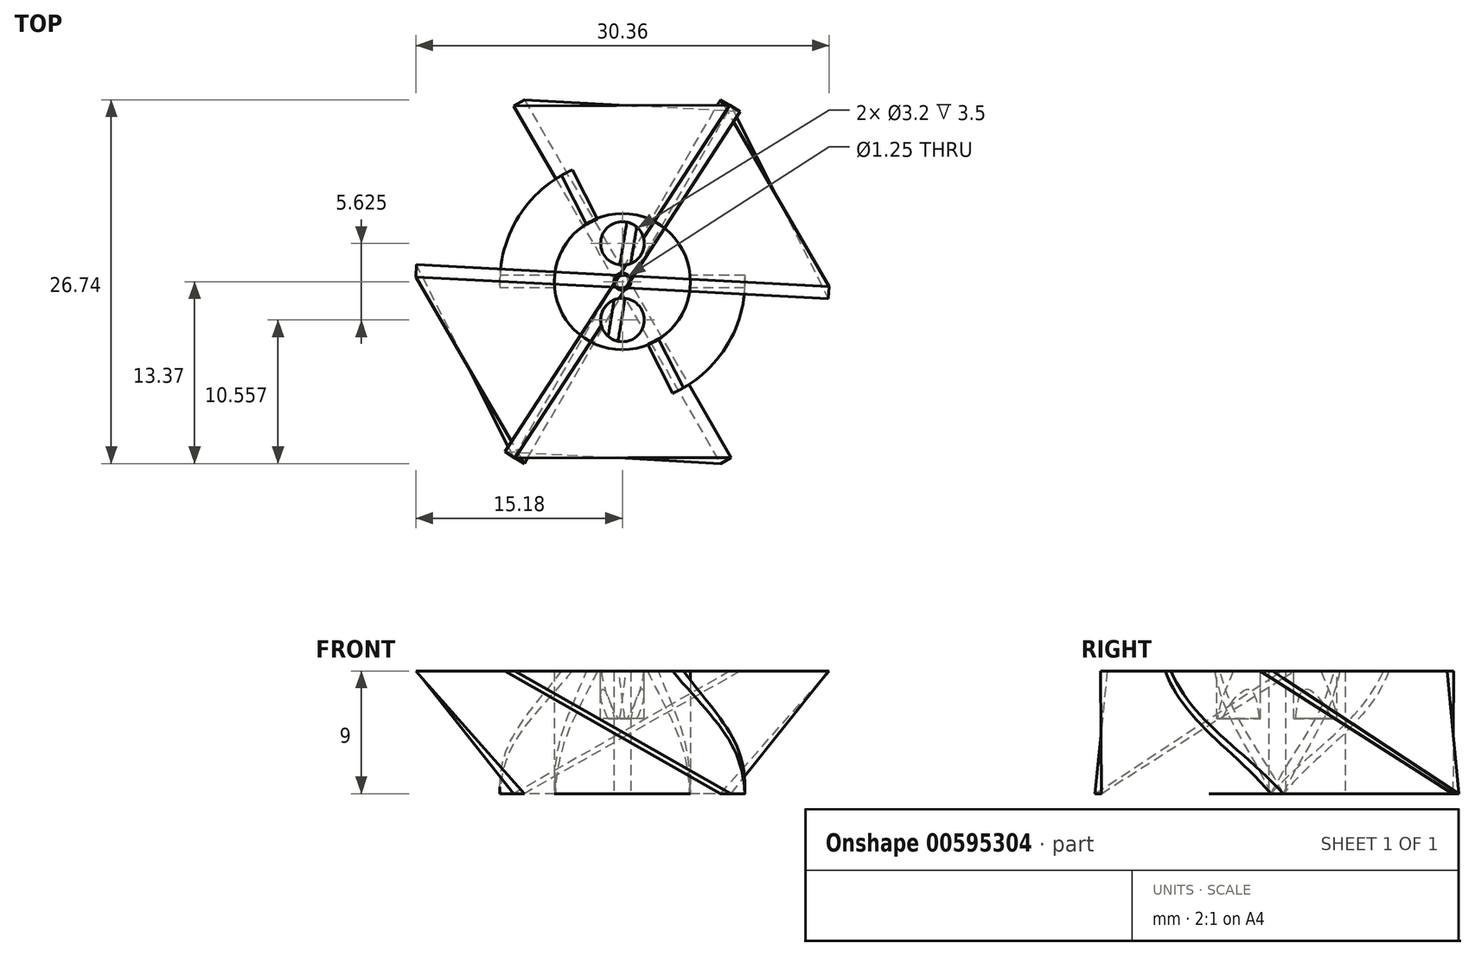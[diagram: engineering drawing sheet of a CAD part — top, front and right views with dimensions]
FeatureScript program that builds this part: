
annotation { "Feature Type Name" : "Feature", "Feature Type Description" : "" }
export const myFeature = defineFeature(function(context is Context, id is Id, definition is map)
    precondition{}
    {
        {
            var Q0;
            Q0=qCreatedBy(makeId("Top.planeOp"),FACE);
            cPlane(context, id + "F0", {"entities" : qUnion([Q0]), "cplaneType" : CPlaneType.OFFSET, "offset" : 9 * mm, "width" : 150 * mm, "height" : 150 * mm});
        }
        {
            var Q0;
            Q0=qCreatedBy(makeId("Top.planeOp"),FACE);
            cPlane(context, id + "F1", {"entities" : qUnion([Q0]), "cplaneType" : CPlaneType.OFFSET, "offset" : 3 * mm, "oppositeDirection" : true, "width" : 150 * mm, "height" : 150 * mm});
        }
        {
            var Q0;
            Q0=qCreatedBy(makeId("Top.planeOp"),FACE);
            var sketch = newSketch(context, id + "F2", { "sketchPlane" : qUnion([Q0])});
            skCircle(sketch, "E0", {"center": v(0, 0) * mm, "radius": 0.63 * mm});
            skCircle(sketch, "E1", {"center": v(0, 0) * mm, "radius": 5 * mm});
            skSolve(sketch);
        }
        {
            var Q0;
            Q0=qCreatedBy(id+"F0.planeOp",FACE);
            var sketch = newSketch(context, id + "F3", { "sketchPlane" : qUnion([Q0])});
            skCircle(sketch, "E2", {"center": v(0, 2.81) * mm, "radius": 1.6 * mm});
            skCircle(sketch, "E3", {"center": v(0, -2.81) * mm, "radius": 1.6 * mm});
            skSolve(sketch);
        }
        {
            var Q0;
            Q0=qCreatedBy(id+"F1.planeOp",FACE);
            var sketch = newSketch(context, id + "F4", { "sketchPlane" : qUnion([Q0])});
            skCircle(sketch, "E4", {"center": v(0, 0) * mm, "radius": 4.95 * mm});
            skCircle(sketch, "E5", {"center": v(0, 0) * mm, "radius": 9 * mm});
            skSolve(sketch);
        }
        {
            var Q0;
            Q0=qCreatedBy(makeId("Top.planeOp"),FACE);
            var sketch = newSketch(context, id + "F5", { "sketchPlane" : qUnion([Q0])});
            skLineSegment(sketch, "E6.bottom", {"start": v(15.18, -0.45) * mm, "end": v(-15.18, -0.45) * mm});
            skLineSegment(sketch, "E6.top", {"start": v(15.18, 0.45) * mm, "end": v(-15.18, 0.45) * mm});
            skLineSegment(sketch, "E6.left", {"start": v(15.18, -0.45) * mm, "end": v(15.18, 0.45) * mm});
            skLineSegment(sketch, "E6.right", {"start": v(-15.18, -0.45) * mm, "end": v(-15.18, 0.45) * mm});
            skPoint(sketch, "E6.middle", {"position": v(0, 0) * mm});
            skSolve(sketch);
        }
        {
            var Q0;
            Q0=qCreatedBy(makeId("Top.planeOp"),FACE);
            var sketch = newSketch(context, id + "F6", { "sketchPlane" : qUnion([Q0])});
            skPoint(sketch, "E7.middle", {"position": v(0, 0) * mm});
            skLineSegment(sketch, "E8.1.0", {"start": v(-7.2, 13.37) * mm, "end": v(7.98, -12.92) * mm});
            skLineSegment(sketch, "E8.1.1", {"start": v(-7.98, 12.92) * mm, "end": v(7.2, -13.37) * mm});
            skLineSegment(sketch, "E8.1.2", {"start": v(-7.2, 13.37) * mm, "end": v(-7.98, 12.92) * mm});
            skLineSegment(sketch, "E8.1.3", {"start": v(7.98, -12.92) * mm, "end": v(7.2, -13.37) * mm});
            skSolve(sketch);
        }
        {
            var Q0;
            Q0=qCreatedBy(makeId("Top.planeOp"),FACE);
            var sketch = newSketch(context, id + "F7", { "sketchPlane" : qUnion([Q0])});
            skPoint(sketch, "E9.middle", {"position": v(0, 0) * mm});
            skLineSegment(sketch, "E10.2.0", {"start": v(-7.98, -12.92) * mm, "end": v(7.2, 13.37) * mm});
            skLineSegment(sketch, "E10.2.1", {"start": v(-7.2, -13.37) * mm, "end": v(7.98, 12.92) * mm});
            skLineSegment(sketch, "E10.2.2", {"start": v(-7.98, -12.92) * mm, "end": v(-7.2, -13.37) * mm});
            skLineSegment(sketch, "E10.2.3", {"start": v(7.2, 13.37) * mm, "end": v(7.98, 12.92) * mm});
            skSolve(sketch);
        }
        {
            var Q0;
            Q0=qCreatedBy(id+"F0.planeOp",FACE);
            var sketch = newSketch(context, id + "F8", { "sketchPlane" : qUnion([Q0])});
            skLineSegment(sketch, "E11.bottom", {"start": v(6.49, -13.73) * mm, "end": v(-7.3, 13.32) * mm});
            skLineSegment(sketch, "E11.top", {"start": v(7.3, -13.32) * mm, "end": v(-6.49, 13.73) * mm});
            skLineSegment(sketch, "E11.left", {"start": v(6.49, -13.73) * mm, "end": v(7.3, -13.32) * mm});
            skLineSegment(sketch, "E11.right", {"start": v(-7.3, 13.32) * mm, "end": v(-6.49, 13.73) * mm});
            skPoint(sketch, "E11.middle", {"position": v(0, 0) * mm});
            skSolve(sketch);
        }
        {
            var Q0;
            Q0=qCreatedBy(id+"F0.planeOp",FACE);
            var sketch = newSketch(context, id + "F9", { "sketchPlane" : qUnion([Q0])});
            skPoint(sketch, "E12.middle", {"position": v(0, 0) * mm});
            skLineSegment(sketch, "E13.1.0", {"start": v(8.64, 12.48) * mm, "end": v(-7.89, -12.97) * mm});
            skLineSegment(sketch, "E13.1.1", {"start": v(7.89, 12.97) * mm, "end": v(-8.64, -12.48) * mm});
            skLineSegment(sketch, "E13.1.2", {"start": v(8.64, 12.48) * mm, "end": v(7.89, 12.97) * mm});
            skLineSegment(sketch, "E13.1.3", {"start": v(-7.89, -12.97) * mm, "end": v(-8.64, -12.48) * mm});
            skSolve(sketch);
        }
        {
            var Q0;
            Q0=qCreatedBy(id+"F0.planeOp",FACE);
            var sketch = newSketch(context, id + "F10", { "sketchPlane" : qUnion([Q0])});
            skPoint(sketch, "E14.middle", {"position": v(0, 0) * mm});
            skLineSegment(sketch, "E15.2.0", {"start": v(-15.13, 1.24) * mm, "end": v(15.18, -0.34) * mm});
            skLineSegment(sketch, "E15.2.1", {"start": v(-15.18, 0.34) * mm, "end": v(15.13, -1.24) * mm});
            skLineSegment(sketch, "E15.2.2", {"start": v(-15.13, 1.24) * mm, "end": v(-15.18, 0.34) * mm});
            skLineSegment(sketch, "E15.2.3", {"start": v(15.18, -0.34) * mm, "end": v(15.13, -1.24) * mm});
            skSolve(sketch);
        }
        {
            var Q0;
            Q0=makeQuery(id+"F5.imprint","IMPRINT",FACE,{"disambiguationData":[TD([[makeQuery(id+"F5.imprint","IMPRINT",EDGE,{"derivedFrom":sQuery(id+"F5.wireOp",EDGE,"E6.bottom")}),-1.0]])]});
            var Q1;
            Q1=makeQuery(id+"F8.imprint","IMPRINT",FACE,{"disambiguationData":[TD([[makeQuery(id+"F8.imprint","IMPRINT",EDGE,{"derivedFrom":sQuery(id+"F8.wireOp",EDGE,"E11.bottom")}),-1.0]])]});
            loft(context, id + "F11", {"sheetProfilesArray" : [{ "sheetProfileEntities" : qUnion([Q0]) }, { "sheetProfileEntities" : qUnion([Q1]) }]});
        }
        {
            var Q0;
            Q0=makeQuery(id+"F9.imprint","IMPRINT",FACE,{"disambiguationData":[TD([[makeQuery(id+"F9.imprint","IMPRINT",EDGE,{"derivedFrom":sQuery(id+"F9.wireOp",EDGE,"E13.1.0")}),-1.0]])]});
            var Q1;
            Q1=makeQuery(id+"F6.imprint","IMPRINT",FACE,{"disambiguationData":[TD([[makeQuery(id+"F6.imprint","IMPRINT",EDGE,{"derivedFrom":sQuery(id+"F6.wireOp",EDGE,"E8.1.0")}),-1.0]])]});
            loft(context, id + "F12", {"sheetProfilesArray" : [{ "sheetProfileEntities" : qUnion([Q0]) }, { "sheetProfileEntities" : qUnion([Q1]) }]});
        }
        {
            var Q0;
            Q0=qSketchRegion(id+"F7",true);
            var Q1;
            Q1=qSketchRegion(id+"F10",true);
            loft(context, id + "F13", {"sheetProfilesArray" : [{ "sheetProfileEntities" : qUnion([Q0]) }, { "sheetProfileEntities" : qUnion([Q1]) }]});
        }
        {
            var Q0;
            Q0=makeQuery(id+"F4.imprint","IMPRINT",FACE,{"disambiguationData":[TD([[makeQuery(id+"F4.imprint","IMPRINT",EDGE,{"derivedFrom":sQuery(id+"F4.wireOp",EDGE,"E4")}),-1.0]])]});
            extrude(context, id + "F14", {"entities" : qUnion([Q0]), "depth" : 25 * mm, "offsetDistance" : 25 * mm});
        }
        {
            var Q0;
            Q0=makeQuery(id+"F11.opLoft","SWEPT_BODY",BODY,{"disambiguationData":[OSD([makeQuery(id+"F5.imprint","IMPRINT",FACE,{"disambiguationData":[TD([[makeQuery(id+"F5.imprint","IMPRINT",EDGE,{"derivedFrom":sQuery(id+"F5.wireOp",EDGE,"E6.bottom")}),-1.0]])]}),makeQuery(id+"F8.imprint","IMPRINT",FACE,{"disambiguationData":[TD([[makeQuery(id+"F8.imprint","IMPRINT",EDGE,{"derivedFrom":sQuery(id+"F8.wireOp",EDGE,"E11.bottom")}),-1.0]])]})])]});
            var Q1;
            Q1=makeQuery(id+"F14.opExtrude","SWEPT_BODY",BODY,{"disambiguationData":[OSD([sQuery(id+"F4.wireOp",EDGE,"E4"),sQuery(id+"F4.wireOp",EDGE,"E5")])]});
            booleanBodies(context, id + "F15", {"operationType" : BooleanOperationType.INTERSECTION, "tools" : qUnion([Q0, Q1])});
        }
        {
            var Q0;
            Q0=makeQuery(id+"F2.imprint","IMPRINT",FACE,{"disambiguationData":[TD([[makeQuery(id+"F2.imprint","IMPRINT",EDGE,{"derivedFrom":sQuery(id+"F2.wireOp",EDGE,"E0")}),-1.0]])]});
            extrude(context, id + "F16", {"entities" : qUnion([Q0]), "depth" : 9 * mm, "offsetDistance" : 25 * mm});
        }
        {
            var Q0;
            Q0=qSketchRegion(id+"F3",true);
            extrude(context, id + "F17", {"entities" : qUnion([Q0]), "operationType" : NewBodyOperationType.REMOVE, "oppositeDirection" : true, "depth" : 3.5 * mm, "offsetDistance" : 25 * mm});
        }
    });
